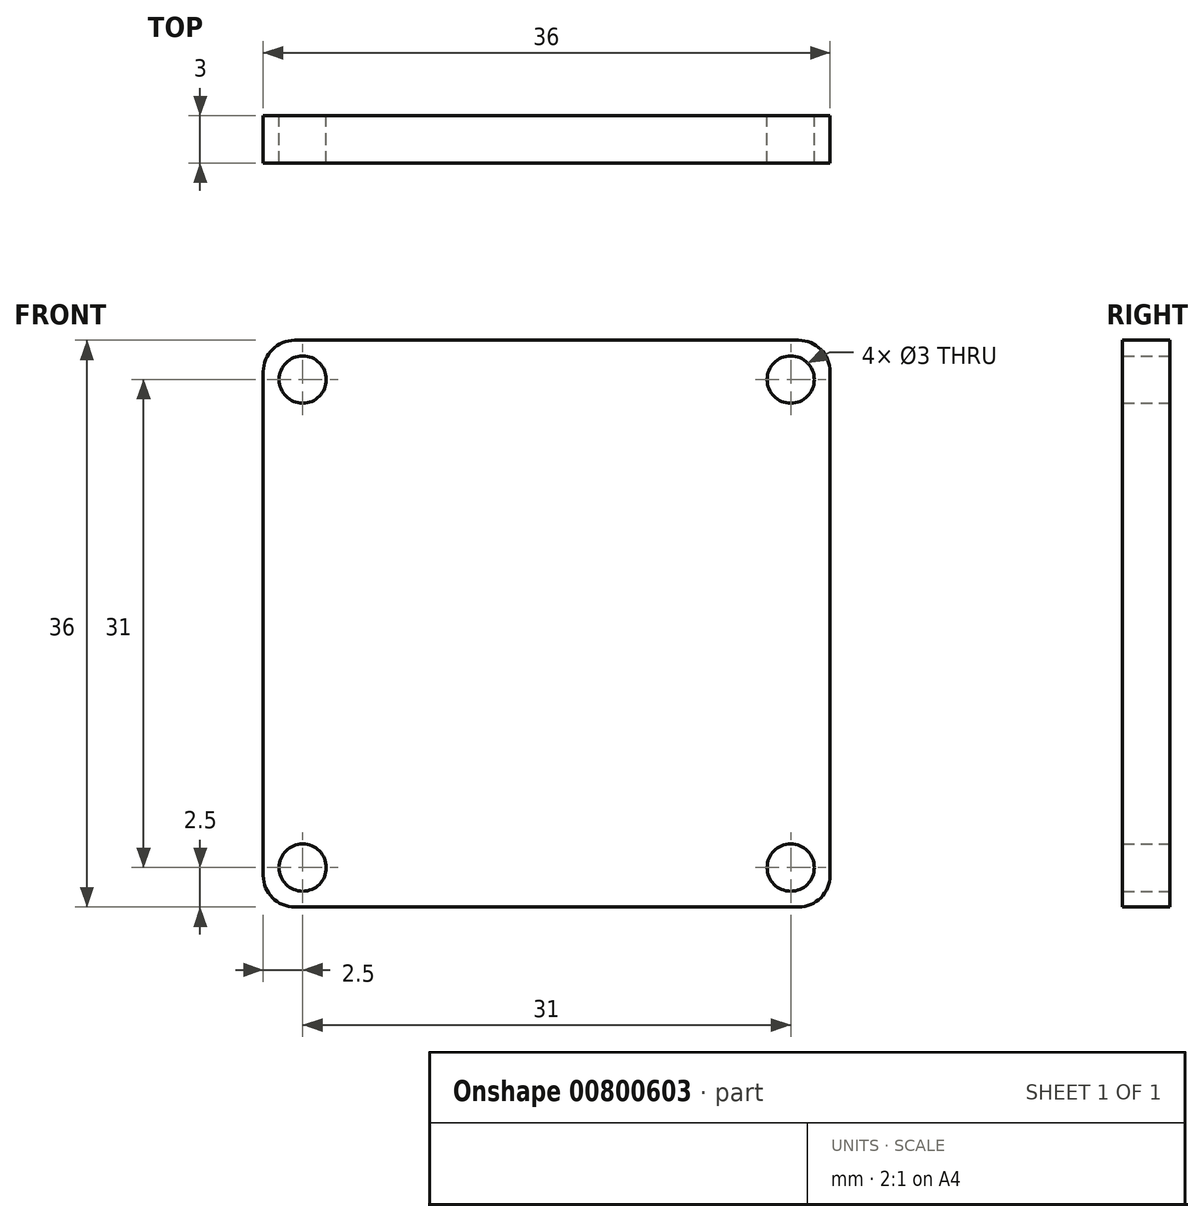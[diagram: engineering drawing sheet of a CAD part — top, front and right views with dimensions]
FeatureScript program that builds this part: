
annotation { "Feature Type Name" : "Feature", "Feature Type Description" : "" }
export const myFeature = defineFeature(function(context is Context, id is Id, definition is map)
    precondition{}
    {
        {
            var Q0;
            Q0=qCreatedBy(makeId("Front.planeOp"),FACE);
            var sketch = newSketch(context, id + "F0", { "sketchPlane" : qUnion([Q0])});
            skLineSegment(sketch, "E0.bottom", {"start": v(-18, 18) * mm, "end": v(18, 18) * mm});
            skLineSegment(sketch, "E0.top", {"start": v(-18, -18) * mm, "end": v(18, -18) * mm});
            skLineSegment(sketch, "E0.left", {"start": v(-18, 18) * mm, "end": v(-18, -18) * mm});
            skLineSegment(sketch, "E0.right", {"start": v(18, 18) * mm, "end": v(18, -18) * mm});
            skPoint(sketch, "E0.middle", {"position": v(0, 0) * mm});
            skCircle(sketch, "E1", {"center": v(-15.5, 15.5) * mm, "radius": 1.5 * mm});
            skCircle(sketch, "E2.MirrorC", {"center": v(15.5, 15.5) * mm, "radius": 1.5 * mm});
            skCircle(sketch, "E3.MirrorC", {"center": v(-15.5, -15.5) * mm, "radius": 1.5 * mm});
            skCircle(sketch, "E4.MirrorC", {"center": v(15.5, -15.5) * mm, "radius": 1.5 * mm});
            skSolve(sketch);
        }
        {
            var Q0;
            Q0 = qSketchRegion(id + "F0", true);
            extrude(context, id + "F1", {"entities" : qUnion([Q0]), "depth" : 3 * mm, "offsetDistance" : 25 * mm});
        }
        {
            var Q0;
            Q0=makeQuery(id+"F1.opExtrude","SWEPT_EDGE",EDGE,{"disambiguationData":[OSD([sQuery(id+"F0.wireOp",EDGE,"E0.bottom"),sQuery(id+"F0.wireOp",EDGE,"E0.left")])]});
            var Q1;
            Q1=makeQuery(id+"F1.opExtrude","SWEPT_EDGE",EDGE,{"disambiguationData":[OSD([sQuery(id+"F0.wireOp",EDGE,"E0.top"),sQuery(id+"F0.wireOp",EDGE,"E0.left")])]});
            var Q2;
            Q2=makeQuery(id+"F1.opExtrude","SWEPT_EDGE",EDGE,{"disambiguationData":[OSD([sQuery(id+"F0.wireOp",EDGE,"E0.top"),sQuery(id+"F0.wireOp",EDGE,"E0.right")])]});
            var Q3;
            Q3=makeQuery(id+"F1.opExtrude","SWEPT_EDGE",EDGE,{"disambiguationData":[OSD([sQuery(id+"F0.wireOp",EDGE,"E0.bottom"),sQuery(id+"F0.wireOp",EDGE,"E0.right")])]});
            fillet(context, id + "F2", {"entities" : qUnion([Q0, Q1, Q2, Q3]), "radius" : 2 * mm, "tangentPropagation" : true, "allowEdgeOverflow" : false});
        }
    });
